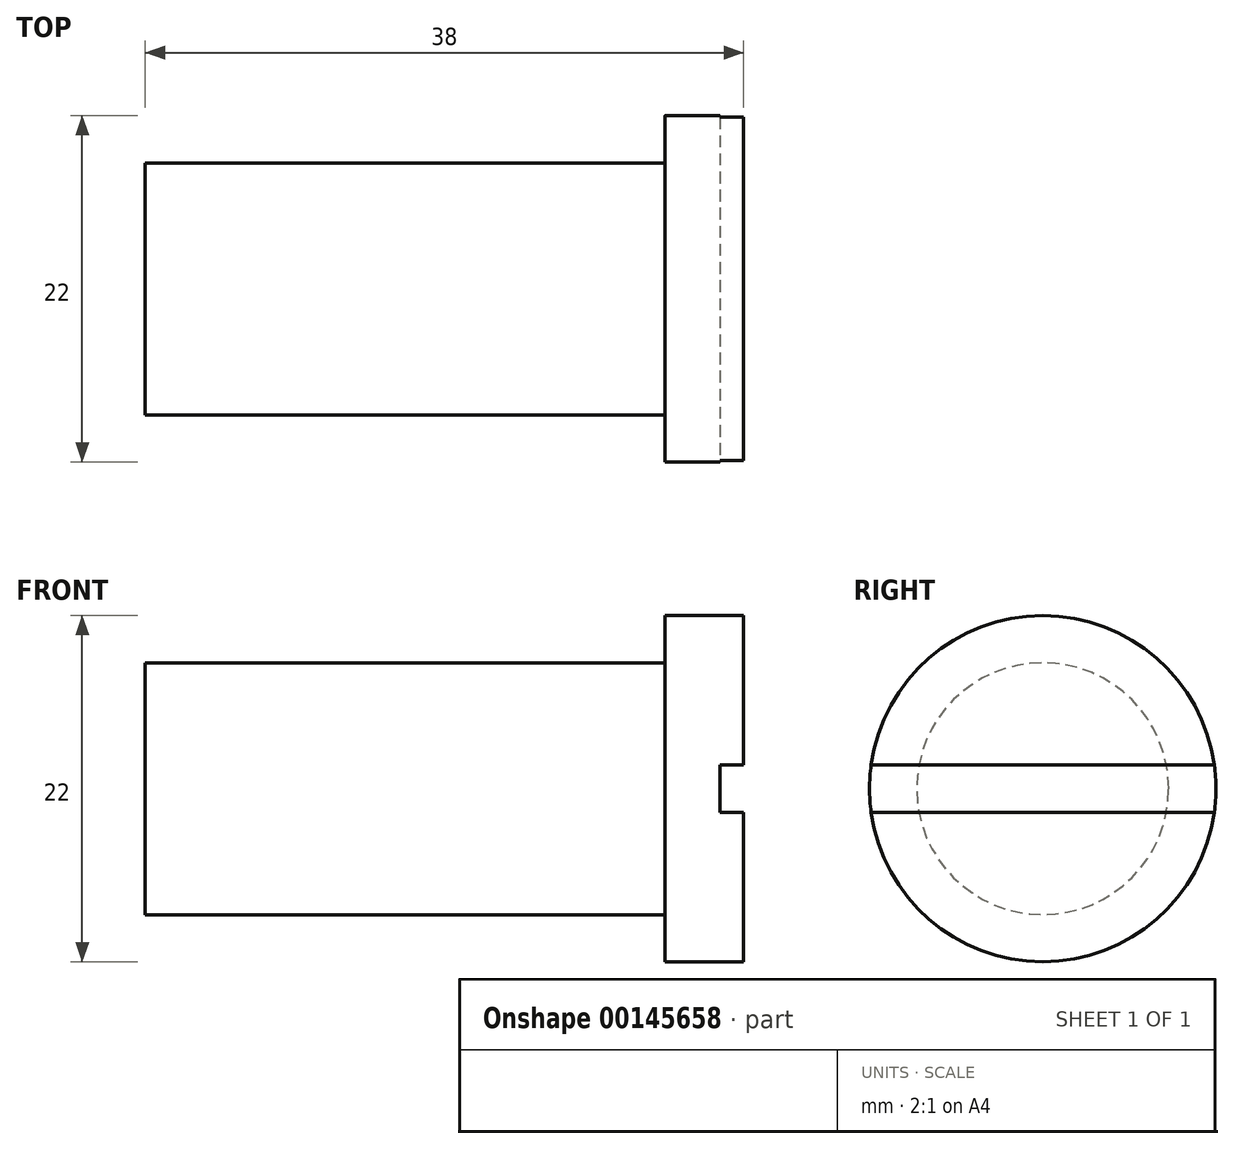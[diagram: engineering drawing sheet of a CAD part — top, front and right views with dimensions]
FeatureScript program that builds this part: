
annotation { "Feature Type Name" : "Feature", "Feature Type Description" : "" }
export const myFeature = defineFeature(function(context is Context, id is Id, definition is map)
    precondition{}
    {
        {
            var Q0;
            Q0=qCreatedBy(makeId("Right.planeOp"),FACE);
            var sketch = newSketch(context, id + "F0", { "sketchPlane" : qUnion([Q0])});
            skCircle(sketch, "E0", {"center": v(0, 0) * mm, "radius": 11 * mm});
            skLineSegment(sketch, "E1", {"start": v(-10.9, -1.5) * mm, "end": v(10.9, -1.5) * mm});
            skLineSegment(sketch, "E2", {"start": v(10.9, 1.5) * mm, "end": v(-10.9, 1.5) * mm});
            skSolve(sketch);
        }
        {
            var Q0;
            Q0=qSketchRegion(id+"F0",true);
            extrude(context, id + "F1", {"entities" : qUnion([Q0]), "depth" : 5 * mm});
        }
        {
            var Q0;
            Q0=makeQuery(id+"F1.opExtrude","CAP_FACE",FACE,{"disambiguationData":[OSD([sQuery(id+"F0.wireOp",EDGE,"E0")])],"isStart":false});
            var sketch = newSketch(context, id + "F2", { "sketchPlane" : qUnion([Q0])});
            skLineSegment(sketch, "E3.0", {"start": v(10.9, 1.5) * mm, "end": v(-10.9, 1.5) * mm});
            skLineSegment(sketch, "E4.0", {"start": v(-10.9, -1.5) * mm, "end": v(10.9, -1.5) * mm});
            skArc(sketch, "E5.0", {"start": v(-10.9, 1.5) * mm, "mid": v(-11, 0) * mm, "end": v(-10.9, -1.5) * mm});
            skArc(sketch, "E6.trimOffspring", {"start": v(10.9, -1.5) * mm, "mid": v(11, 0) * mm, "end": v(10.9, 1.5) * mm});
            skSolve(sketch);
        }
        {
            var Q0;
            Q0=qSketchRegion(id+"F2",true);
            extrude(context, id + "F3", {"entities" : qUnion([Q0]), "operationType" : NewBodyOperationType.REMOVE, "oppositeDirection" : true, "depth" : 1.5 * mm});
        }
        {
            var Q0;
            {var subQ0=sQuery(id+"F0.wireOp",EDGE,"E2");Q0=makeQuery(id+"F0.imprint","IMPRINT",FACE,{"disambiguationData":[TD([[makeQuery(id+"F0.imprint","IMPRINT",EDGE,{"derivedFrom":subQ0}),-1.0]])]});}
            var sketch = newSketch(context, id + "F4", { "sketchPlane" : qUnion([Q0])});
            skCircle(sketch, "E7", {"center": v(0, 0) * mm, "radius": 8 * mm});
            skSolve(sketch);
        }
        {
            var Q0;
            Q0=qSketchRegion(id+"F4",true);
            extrude(context, id + "F5", {"entities" : qUnion([Q0]), "operationType" : NewBodyOperationType.ADD, "oppositeDirection" : true, "depth" : 33 * mm});
        }
    });
